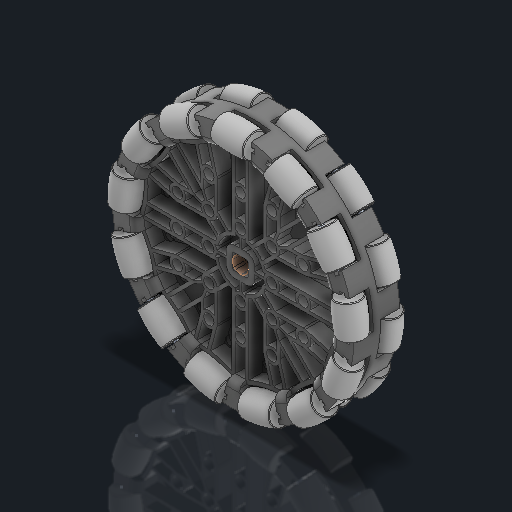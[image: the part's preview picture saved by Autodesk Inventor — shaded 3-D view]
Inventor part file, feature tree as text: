
AUTODESK INVENTOR PART (.ipt)
format: ipt  version: 2023.2 (Build 272271030, 271C)  size: 4,788,224 bytes
history: native  units: in
note: dims shown in document units (in); Inventor stores cm internally (conversion verified against a paired STEP export)
features: other x55, move_body x1, sketch x1, extrude x1
ambient origin geometry x8: Origin, YZ Plane, XZ Plane, XY Plane, X Axis, Y Axis, Z Axis, Center Point
bodies: Solid1 (feature_tree), Solid2 (feature_tree), Solid3 (feature_tree), Solid4 (feature_tree), Solid5 (feature_tree), Solid6 (feature_tree), Solid7 (feature_tree), Solid8 (feature_tree), Solid9 (feature_tree), Solid10 (feature_tree), Solid11 (feature_tree), Solid12 (feature_tree), Solid13 (feature_tree), Solid14 (feature_tree), Solid15 (feature_tree), Solid16 (feature_tree), Solid17 (feature_tree), Solid18 (feature_tree), Solid19 (feature_tree), Solid20 (feature_tree), Solid21 (feature_tree), Solid22 (feature_tree), Solid23 (feature_tree), Solid24 (feature_tree), Solid25 (feature_tree), Solid26 (feature_tree), Solid27 (feature_tree), Solid28 (feature_tree), Solid29 (feature_tree), Solid30 (feature_tree), Solid31 (feature_tree), Solid32 (feature_tree), Solid33 (feature_tree), Solid34 (feature_tree), Solid35 (feature_tree), Solid36 (feature_tree), Solid37 (feature_tree), Solid38 (feature_tree), Solid39 (feature_tree), Solid40 (feature_tree), Solid41 (feature_tree), Solid42 (feature_tree), Solid43 (feature_tree), Solid44 (feature_tree), Solid45 (feature_tree), Solid46 (feature_tree), Solid47 (feature_tree), Solid48 (feature_tree), Solid49 (feature_tree), Solid50 (feature_tree), Solid51 (feature_tree), Solid52 (feature_tree), Solid53 (feature_tree)
feature tree (58):
  other  "4 (320mm Travel) Omni-Directional Anti-Static Wheel (276-8107).iam"
  other  "276-8107-001 Web.ipt:1"
  other  "276-8107-002 Web.iam:1::276-3526-001 Web.ipt:1"
  other  "276-8107-002 Web.iam:1::276-8107-003 Web.ipt:1"
  other  "276-8107-002 Web_1.iam:1::276-3526-001 Web.ipt:1"
  other  "276-8107-002 Web_1.iam:1::276-8107-003 Web.ipt:1"
  other  "276-8107-002 Web_2.iam:1::276-3526-001 Web.ipt:1"
  other  "276-8107-002 Web_2.iam:1::276-8107-003 Web.ipt:1"
  other  "276-8107-002 Web_3.iam:1::276-3526-001 Web.ipt:1"
  other  "276-8107-002 Web_3.iam:1::276-8107-003 Web.ipt:1"
  other  "276-8107-002 Web_4.iam:1::276-3526-001 Web.ipt:1"
  other  "276-8107-002 Web_4.iam:1::276-8107-003 Web.ipt:1"
  other  "276-8107-002 Web_5.iam:1::276-3526-001 Web.ipt:1"
  other  "276-8107-002 Web_5.iam:1::276-8107-003 Web.ipt:1"
  other  "276-8107-002 Web_6.iam:1::276-3526-001 Web.ipt:1"
  other  "276-8107-002 Web_6.iam:1::276-8107-003 Web.ipt:1"
  other  "276-8107-002 Web_7.iam:1::276-3526-001 Web.ipt:1"
  other  "276-8107-002 Web_7.iam:1::276-8107-003 Web.ipt:1"
  other  "276-8107-002 Web_8.iam:1::276-3526-001 Web.ipt:1"
  other  "276-8107-002 Web_8.iam:1::276-8107-003 Web.ipt:1"
  other  "276-8107-002 Web_9.iam:1::276-3526-001 Web.ipt:1"
  other  "276-8107-002 Web_9.iam:1::276-8107-003 Web.ipt:1"
  other  "276-8107-002 Web_10.iam:1::276-3526-001 Web.ipt:1"
  other  "276-8107-002 Web_10.iam:1::276-8107-003 Web.ipt:1"
  other  "276-8107-002 Web_11.iam:1::276-3526-001 Web.ipt:1"
  other  "276-8107-002 Web_11.iam:1::276-8107-003 Web.ipt:1"
  other  "276-8107-002 Web_12.iam:1::276-3526-001 Web.ipt:1"
  other  "276-8107-002 Web_12.iam:1::276-8107-003 Web.ipt:1"
  other  "276-8107-002 Web_13.iam:1::276-3526-001 Web.ipt:1"
  other  "276-8107-002 Web_13.iam:1::276-8107-003 Web.ipt:1"
  other  "276-8107-002 Web_14.iam:1::276-3526-001 Web.ipt:1"
  other  "276-8107-002 Web_14.iam:1::276-8107-003 Web.ipt:1"
  other  "276-8107-002 Web_15.iam:1::276-3526-001 Web.ipt:1"
  other  "276-8107-002 Web_15.iam:1::276-8107-003 Web.ipt:1"
  other  "276-8107-002 Web_16.iam:1::276-3526-001 Web.ipt:1"
  other  "276-8107-002 Web_16.iam:1::276-8107-003 Web.ipt:1"
  other  "276-8107-002 Web_17.iam:1::276-3526-001 Web.ipt:1"
  other  "276-8107-002 Web_17.iam:1::276-8107-003 Web.ipt:1"
  other  "276-8107-002 Web_18.iam:1::276-3526-001 Web.ipt:1"
  other  "276-8107-002 Web_18.iam:1::276-8107-003 Web.ipt:1"
  other  "276-8107-002 Web_19.iam:1::276-3526-001 Web.ipt:1"
  other  "276-8107-002 Web_19.iam:1::276-8107-003 Web.ipt:1"
  other  "276-8107-002 Web_20.iam:1::276-3526-001 Web.ipt:1"
  other  "276-8107-002 Web_20.iam:1::276-8107-003 Web.ipt:1"
  other  "276-8107-002 Web_21.iam:1::276-3526-001 Web.ipt:1"
  other  "276-8107-002 Web_21.iam:1::276-8107-003 Web.ipt:1"
  other  "276-8107-002 Web_22.iam:1::276-3526-001 Web.ipt:1"
  other  "276-8107-002 Web_22.iam:1::276-8107-003 Web.ipt:1"
  other  "276-8107-002 Web_23.iam:1::276-3526-001 Web.ipt:1"
  other  "276-8107-002 Web_23.iam:1::276-8107-003 Web.ipt:1"
  other  "276-8107-002 Web_24.iam:1::276-3526-001 Web.ipt:1"
  other  "276-8107-002 Web_24.iam:1::276-8107-003 Web.ipt:1"
  other  "276-8107-002 Web_25.iam:1::276-3526-001 Web.ipt:1"
  other  "276-8107-002 Web_25.iam:1::276-8107-003 Web.ipt:1"
  move_body  "Move Body1"
  sketch  "Sketch1"  dims[d0=0.3937in d1=90.0deg d2=0.25in d3=1.0in d4=0.0in]
  other  "Srf1"
  extrude  "ExtrusionSrf1"  TaperAngle=90.0deg  [1 undecoded]
note: 1 required parameter value undecoded (feature->parameter linkage not recoverable at this tier; creation-order binding heuristic only, values carry confidence <= 0.55)
